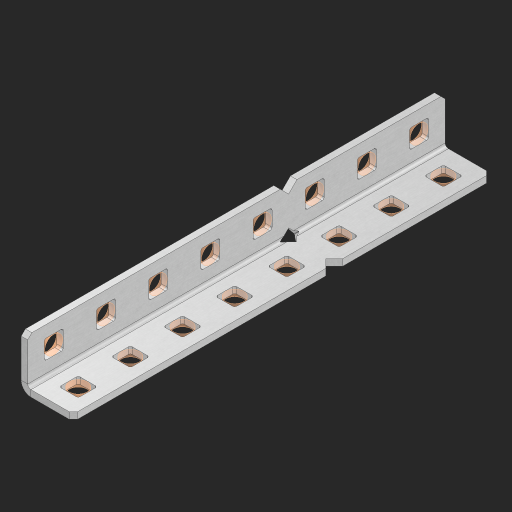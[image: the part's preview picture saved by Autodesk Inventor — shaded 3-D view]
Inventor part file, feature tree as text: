
AUTODESK INVENTOR PART (.ipt)
format: ipt  version: 2023 (Build 270158000, 158)  size: 562,688 bytes
history: native  units: in
note: dims shown in document units (in); Inventor stores cm internally (conversion verified against a paired STEP export)
features: other x22, extrude x17, sheet_metal_op x8, sketch x5, pattern_linear x1, mirror x1, chamfer x1
ambient origin geometry x8: Origin, YZ Plane, XZ Plane, XY Plane, X Axis, Y Axis, Z Axis, Center Point
bodies: Solid1 (feature_tree), Body (feature_tree)
feature tree (55):
  sheet_metal_op  "Flanges"
  sheet_metal_op  "Body Pattern"
  other  "Arc Length"
  pattern_linear  "Notch Pattern"  Spacing1=0.125in  [1 undecoded]
  other  "Diagonal Plane"
  mirror  "Everything Mirrored"
  chamfer  "End Chamfer"
  sketch  "Sketch1"  dims[d0=0.5in]
  other  "Plate1"
  sketch  "Sketch2"  dims[d1=4.0in]
  other  "Plate2"
  sheet_metal_op  "Bend1"
  sheet_metal_op  "Corner1"
  sketch  "Sketch8"  dims[d2=0.0625in]
  sketch  "Sketch9"  dims[d3=0.0625in]
  other  "Srf91"
  sheet_metal_op  "Body Pattern Sketch"
  other  "Srf92"
  sketch  "Sketch13"  dims[d4=0.0312in d5=0.125in d6=0.0625in d7=0.5in d8=90.0deg d9=0.0312in d10=0.25in d11=0.0625in d12=0.0625in d49=0.182in d50=0.02in d52=0.25in d53=0.0625in d54=0.0in d55=0.172in d56=1.0in d57=0.0in d85=0.1473in d86=0.1782in d89=0.0625in d90=0.0in d91=0.04in d92=0.0491in d95=2.5in d96=0.04in d97=0.25in d98=45.0deg d123=0.204in d126=0.0491in d127=0.1473in d128=0.08in d129=0.04in d130=2.5in d131=3.1496in d133=0.5in d134=0.3937in d136=1.0in]
  other  "Srf856"
  other  "Srf857"
  other  "Srf858"
  other  "Srf859"
  other  "Srf860"
  other  "Srf861"
  other  "Srf1275"
  other  "Srf1276"
  other  "Srf1278"
  other  "Srf1279"
  other  "Srf1280"
  other  "Srf1281"
  other  "Srf1282"
  other  "Srf1283"
  other  "Srf1383"
  other  "Srf1475"
  sheet_metal_op  "Body Stamp"
  sheet_metal_op  "Body Circle"
  sheet_metal_op  "Notch"
  extrude  "ExtrusionSrf92"  Depth=0.0625in
  extrude  "ExtrusionSrf856"  Depth=0.5in TaperAngle=90.0deg
  extrude  "ExtrusionSrf857"  Depth=0.3937in
  extrude  "ExtrusionSrf858"  Depth=0.0625in
  extrude  "ExtrusionSrf859"  Depth=0.0625in
  extrude  "ExtrusionSrf860"  Depth=0.3937in
  extrude  "ExtrusionSrf861"  Depth=0.02in
  extrude  "ExtrusionSrf1275"  Depth=0.3937in
  extrude  "ExtrusionSrf1276"  Depth=0.0625in
  extrude  "ExtrusionSrf1277"  TaperAngle=0.0deg  [1 undecoded]
  extrude  "ExtrusionSrf1278"  Depth=0.3937in
  extrude  "ExtrusionSrf1279"  Depth=0.3937in TaperAngle=0.0deg
  extrude  "ExtrusionSrf1280"  Depth=0.3937in
  extrude  "ExtrusionSrf1281"  Depth=0.3937in
  extrude  "ExtrusionSrf1282"  Depth=0.0625in
  extrude  "ExtrusionSrf1383"  Depth=0.3937in TaperAngle=0.0deg
  extrude  "ExtrusionSrf1475"  Depth=0.3937in
note: 2 required parameter values undecoded (feature->parameter linkage not recoverable at this tier; creation-order binding heuristic only, values carry confidence <= 0.55)
